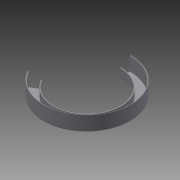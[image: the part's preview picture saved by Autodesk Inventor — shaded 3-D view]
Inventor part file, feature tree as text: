
AUTODESK INVENTOR PART (.ipt)
format: ipt  version: 2015 (Build 190159000, 159)  size: 123,392 bytes
history: native  units: in
note: dims shown in document units (in); Inventor stores cm internally (conversion verified against a paired STEP export)
features: revolve x1, fillet x1, sketch x1
ambient origin geometry x8: Origin, YZ Plane, XZ Plane, XY Plane, X Axis, Y Axis, Z Axis, Center Point
bodies: Solid1 (feature_tree)
feature tree (3):
  revolve  "Revolution1"  [1 undecoded]
  fillet  "Fillet1"  Radius=1.75in
  sketch  "Sketch1"  dims[d3=0.125in d10=1.45in d11=1.75in d12=2.5in d13=0.0625in d14=0.125in d15=0.0625in d16=0.125in d17=1.325in d18=1.5in d19=5.5in d20=2.2in d21=240.0deg d22=0.25in]
note: 1 required parameter value undecoded (feature->parameter linkage not recoverable at this tier; creation-order binding heuristic only, values carry confidence <= 0.55)
